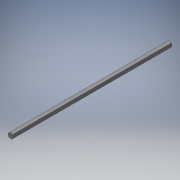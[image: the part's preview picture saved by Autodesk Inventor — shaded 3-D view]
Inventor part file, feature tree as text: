
AUTODESK INVENTOR PART (.ipt)
format: ipt  version: 2018 (Build 220112000, 112)  size: 97,792 bytes
history: native  units: in
note: dims shown in document units (in); Inventor stores cm internally (conversion verified against a paired STEP export)
features: extrude x1, sketch x1
ambient origin geometry x8: Origin, YZ Plane, XZ Plane, XY Plane, X Axis, Y Axis, Z Axis, Center Point
bodies: Solid1 (feature_tree)
feature tree (2):
  extrude  "Extrusion1"  Depth=0.5in
  sketch  "Sketch1"  dims[d1=16.0in d2=0.0in d3=0.5in]
